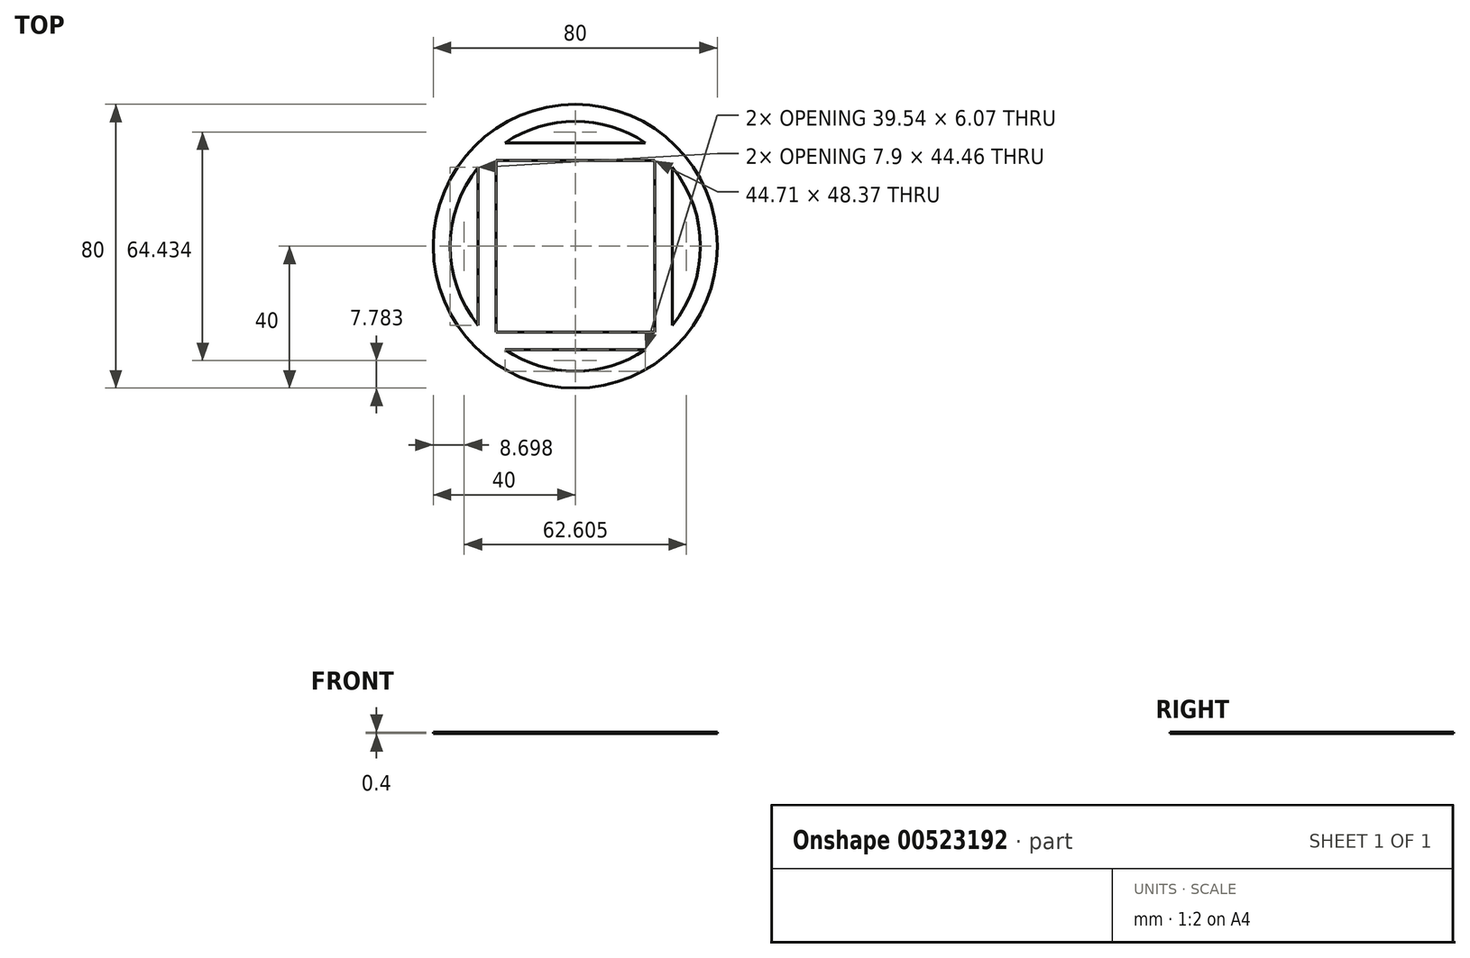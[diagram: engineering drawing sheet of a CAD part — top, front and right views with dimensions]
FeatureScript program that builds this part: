
annotation { "Feature Type Name" : "Feature", "Feature Type Description" : "" }
export const myFeature = defineFeature(function(context is Context, id is Id, definition is map)
    precondition{}
    {
        {
            var Q0;
            Q0=qCreatedBy(makeId("Top.planeOp"),FACE);
            var sketch = newSketch(context, id + "F0", { "sketchPlane" : qUnion([Q0])});
            skCircle(sketch, "E0", {"center": v(0, 0) * mm, "radius": 40 * mm});
            skSolve(sketch);
        }
        {
            var Q0;
            Q0 = qSketchRegion(id + "F0", true);
            extrude(context, id + "F1", {"entities" : qUnion([Q0]), "depth" : 0.4 * mm, "offsetDistance" : 25 * mm});
        }
        {
            var Q0;
            Q0=makeQuery(id+"F1.opExtrude","CAP_FACE",FACE,{"disambiguationData":[OSD([sQuery(id+"F0.wireOp",EDGE,"E0")])],"isStart":false});
            var sketch = newSketch(context, id + "F2", { "sketchPlane" : qUnion([Q0])});
            skLineSegment(sketch, "E1.bottom", {"start": v(-27.35, 29.18) * mm, "end": v(27.35, 29.18) * mm});
            skLineSegment(sketch, "E1.top", {"start": v(-27.35, -29.18) * mm, "end": v(27.35, -29.18) * mm});
            skLineSegment(sketch, "E1.left", {"start": v(-27.35, 29.18) * mm, "end": v(-27.35, -29.18) * mm});
            skLineSegment(sketch, "E1.right", {"start": v(27.35, 29.18) * mm, "end": v(27.35, -29.18) * mm});
            skLineSegment(sketch, "E2.0", {"start": v(-22.35, 24.18) * mm, "end": v(22.35, 24.18) * mm});
            skLineSegment(sketch, "E2.1", {"start": v(-22.35, 24.18) * mm, "end": v(-22.35, -24.18) * mm});
            skLineSegment(sketch, "E2.2", {"start": v(-22.35, -24.18) * mm, "end": v(22.35, -24.18) * mm});
            skLineSegment(sketch, "E2.3", {"start": v(22.35, 24.18) * mm, "end": v(22.35, -24.18) * mm});
            skCircle(sketch, "E3.0", {"center": v(0, 0) * mm, "radius": 40.25 * mm});
            skCircle(sketch, "E4.0", {"center": v(0, 0) * mm, "radius": 35.25 * mm});
            skSolve(sketch);
        }
        {
            var Q0;
            Q0=makeQuery(id+"F2.imprint","IMPRINT",FACE,{"disambiguationData":[TD([[makeQuery(id+"F2.imprint","IMPRINT",EDGE,{"derivedFrom":sQuery(id+"F2.wireOp",EDGE,"E2.0")}),-1.0]])]});
            var Q1;
            {var subQ0=sQuery(id+"F2.wireOp",EDGE,"E4.0");var subQ1=sQuery(id+"F2.wireOp",EDGE,"E1.left");var subQ2=makeQuery(id+"F2.imprint","INTERSECT",VERTEX,{"disambiguationData":[OD(0.0)],"derivedFrom":[subQ1,subQ0]});Q1=makeQuery(id+"F2.imprint","IMPRINT",FACE,{"disambiguationData":[TD([[makeQuery(id+"F2.imprint","IMPRINT",EDGE,{"disambiguationData":[TD([[subQ2,-1.0]])],"derivedFrom":subQ1}),-1.0]])]});}
            var Q2;
            {var subQ0=sQuery(id+"F2.wireOp",EDGE,"E4.0");var subQ1=sQuery(id+"F2.wireOp",EDGE,"E1.bottom");var subQ2=makeQuery(id+"F2.imprint","INTERSECT",VERTEX,{"disambiguationData":[OD(0.0)],"derivedFrom":[subQ1,subQ0]});Q2=makeQuery(id+"F2.imprint","IMPRINT",FACE,{"disambiguationData":[TD([[makeQuery(id+"F2.imprint","IMPRINT",EDGE,{"disambiguationData":[TD([[subQ2,-1.0]])],"derivedFrom":subQ1}),1.0]])]});}
            var Q3;
            {var subQ0=sQuery(id+"F2.wireOp",EDGE,"E4.0");var subQ1=sQuery(id+"F2.wireOp",EDGE,"E1.right");var subQ2=makeQuery(id+"F2.imprint","INTERSECT",VERTEX,{"disambiguationData":[OD(0.0)],"derivedFrom":[subQ1,subQ0]});Q3=makeQuery(id+"F2.imprint","IMPRINT",FACE,{"disambiguationData":[TD([[makeQuery(id+"F2.imprint","IMPRINT",EDGE,{"disambiguationData":[TD([[subQ2,-1.0]])],"derivedFrom":subQ1}),1.0]])]});}
            var Q4;
            {var subQ0=sQuery(id+"F2.wireOp",EDGE,"E4.0");var subQ1=sQuery(id+"F2.wireOp",EDGE,"E1.top");var subQ2=makeQuery(id+"F2.imprint","INTERSECT",VERTEX,{"disambiguationData":[OD(0.0)],"derivedFrom":[subQ1,subQ0]});Q4=makeQuery(id+"F2.imprint","IMPRINT",FACE,{"disambiguationData":[TD([[makeQuery(id+"F2.imprint","IMPRINT",EDGE,{"disambiguationData":[TD([[subQ2,-1.0]])],"derivedFrom":subQ1}),-1.0]])]});}
            extrude(context, id + "F3", {"entities" : qUnion([Q0, Q1, Q2, Q3, Q4]), "operationType" : NewBodyOperationType.REMOVE, "oppositeDirection" : true, "depth" : 25 * mm, "offsetDistance" : 25 * mm});
        }
    });
